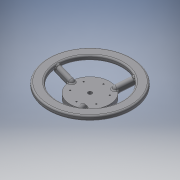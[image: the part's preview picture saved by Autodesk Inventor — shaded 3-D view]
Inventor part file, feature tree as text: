
AUTODESK INVENTOR PART (.ipt)
format: ipt  version: 2017 (Build 210142000, 142)  size: 766,464 bytes
history: native  units: mm
features: reference x6, extrude x3, sketch x3, fillet x2, chamfer x2, other x2, plane x1, pattern_circular x1
ambient origin geometry x8: Origin, YZ Plane, XZ Plane, XY Plane, X Axis, Y Axis, Z Axis, Center Point
bodies: Solid1 (feature_tree)
feature tree (20):
  extrude  "Extrusion1"  Depth=20.0mm
  plane  "Work Plane1"
  extrude  "Extrusion2"  Depth=80.0mm
  extrude  "Extrusion3"  Depth=10.0mm TaperAngle=0.0deg
  pattern_circular  "Circular Pattern1"  [2 undecoded]
  fillet  "Fillet1"  Radius=170.0mm
  fillet  "Fillet2"  Radius=20.0mm
  chamfer  "Chamfer1"  Distance=10.0mm
  chamfer  "Chamfer2"  Distance=10.0mm
  sketch  "Sketch1"  dims[d0=8.0mm d1=20.0mm]
  sketch  "Sketch2"  dims[d2=20.0mm d3=80.0mm]
  sketch  "Sketch3"  dims[d4=4.5mm d5=10.0mm d6=0.0mm d7=10.0mm d8=170.0mm d9=20.0mm d10=10.0mm d11=0.0mm d12=10.0mm d13=0.0mm d14=30.0mm d15=360.0deg d17=5.0mm d18=3.0mm d19=15.0mm d20=2.0mm d21=2.0mm d22=45.0deg d23=2.0mm d24=2.0mm d25=45.0deg]
  reference  "Reference1"
  reference  "Reference2"
  reference  "Reference3"
  reference  "Reference4"
  reference  "Reference5"
  reference  "Reference6"
  other  "peristaltic pump.iam"
  other  "rotor 1:1"
note: 2 required parameter values undecoded (feature->parameter linkage not recoverable at this tier; creation-order binding heuristic only, values carry confidence <= 0.55)
